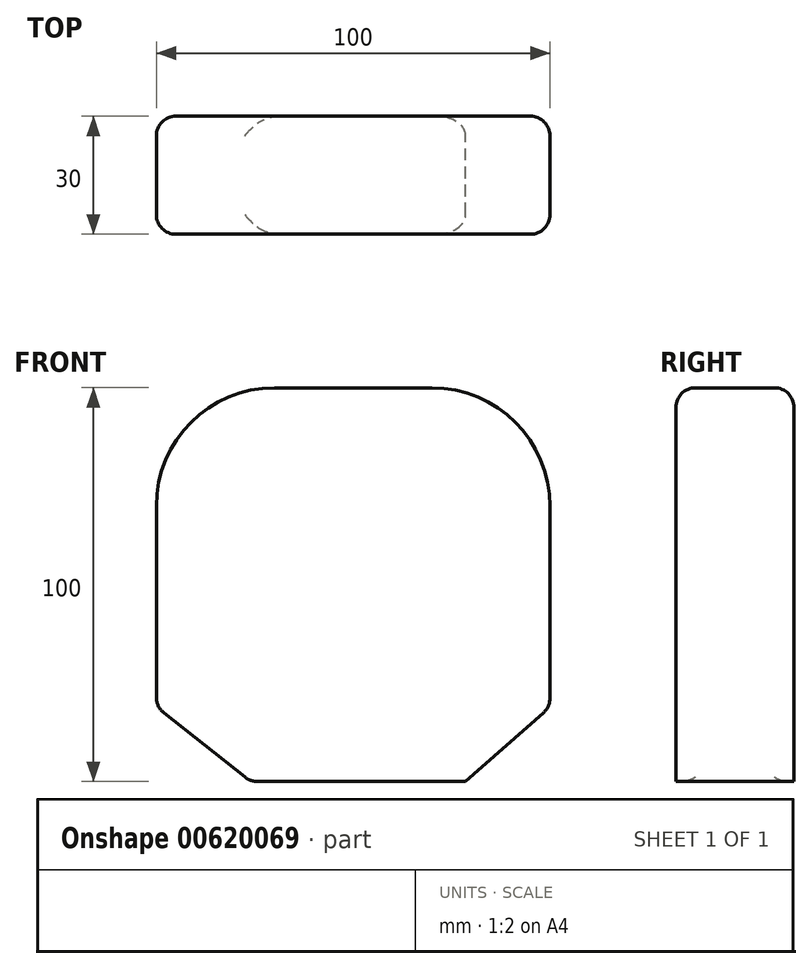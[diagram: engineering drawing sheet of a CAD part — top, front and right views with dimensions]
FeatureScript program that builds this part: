
annotation { "Feature Type Name" : "Feature", "Feature Type Description" : "" }
export const myFeature = defineFeature(function(context is Context, id is Id, definition is map)
    precondition{}
    {
        {
            var Q0;
            Q0=qCreatedBy(makeId("Front.planeOp"),FACE);
            var sketch = newSketch(context, id + "F0", { "sketchPlane" : qUnion([Q0])});
            skLineSegment(sketch, "E0.bottom", {"start": v(-36.15, 40.55) * mm, "end": v(3.85, 40.55) * mm});
            skLineSegment(sketch, "E0.top", {"start": v(-42.3, -59.45) * mm, "end": v(12.4, -59.45) * mm});
            skLineSegment(sketch, "E0.left", {"start": v(-66.15, 10.55) * mm, "end": v(-66.15, -40.55) * mm});
            skLineSegment(sketch, "E0.right", {"start": v(33.85, 10.55) * mm, "end": v(33.85, -40.55) * mm});
            skPoint(sketch, "E1.visualSharp", {"position": v(-66.15, 40.55) * mm});
            skArc(sketch, "E1.filletArc", {"start": v(-36.15, 40.55) * mm, "mid": v(-57.36, 31.76) * mm, "end": v(-66.15, 10.55) * mm});
            skPoint(sketch, "E2.visualSharp", {"position": v(33.85, 40.55) * mm});
            skArc(sketch, "E2.filletArc", {"start": v(33.85, 10.55) * mm, "mid": v(25.06, 31.76) * mm, "end": v(3.85, 40.55) * mm});
            skLineSegment(sketch, "E3", {"start": v(12.4, -59.45) * mm, "end": v(33.85, -40.55) * mm});
            skLineSegment(sketch, "E4", {"start": v(-42.3, -59.45) * mm, "end": v(-66.15, -40.55) * mm});
            skPoint(sketch, "E5.orphan", {"position": v(33.85, -59.45) * mm});
            skSolve(sketch);
        }
        {
            var Q0;
            Q0 = qSketchRegion(id + "F0", true);
            extrude(context, id + "F1", {"entities" : qUnion([Q0]), "depth" : 30 * mm, "offsetDistance" : 25 * mm});
        }
        {
            var Q0;
            Q0=makeQuery(id+"F1.opExtrude","CAP_EDGE",EDGE,{"disambiguationData":[OSD([sQuery(id+"F0.wireOp",EDGE,"E1.filletArc")])],"isStart":false});
            var Q1;
            Q1=makeQuery(id+"F1.opExtrude","SWEPT_FACE",FACE,{"disambiguationData":[OSD([sQuery(id+"F0.wireOp",EDGE,"E1.filletArc")])]});
            var Q2;
            Q2=makeQuery(id+"F1.opExtrude","CAP_EDGE",EDGE,{"disambiguationData":[OSD([sQuery(id+"F0.wireOp",EDGE,"E2.filletArc")])],"isStart":false});
            var Q3;
            Q3=makeQuery(id+"F1.opExtrude","SWEPT_FACE",FACE,{"disambiguationData":[OSD([sQuery(id+"F0.wireOp",EDGE,"E2.filletArc")])]});
            var Q4;
            Q4=makeQuery(id+"F1.opExtrude","CAP_EDGE",EDGE,{"disambiguationData":[OSD([sQuery(id+"F0.wireOp",EDGE,"E3")])],"isStart":false});
            var Q5;
            Q5=makeQuery(id+"F1.opExtrude","SWEPT_EDGE",EDGE,{"disambiguationData":[OSD([sQuery(id+"F0.wireOp",EDGE,"E0.right"),sQuery(id+"F0.wireOp",EDGE,"E3")])]});
            var Q6;
            Q6=makeQuery(id+"F1.opExtrude","CAP_EDGE",EDGE,{"disambiguationData":[OSD([sQuery(id+"F0.wireOp",EDGE,"E4")])],"isStart":false});
            var Q7;
            Q7=makeQuery(id+"F1.opExtrude","CAP_EDGE",EDGE,{"disambiguationData":[OSD([sQuery(id+"F0.wireOp",EDGE,"E4")])],"isStart":true});
            var Q8;
            Q8=makeQuery(id+"F1.opExtrude","SWEPT_FACE",FACE,{"disambiguationData":[OSD([sQuery(id+"F0.wireOp",EDGE,"E4")])]});
            var Q9;
            Q9=makeQuery(id+"F1.opExtrude","CAP_EDGE",EDGE,{"disambiguationData":[OSD([sQuery(id+"F0.wireOp",EDGE,"E3")])],"isStart":true});
            fillet(context, id + "F2", {"entities" : qUnion([Q0, Q1, Q2, Q3, Q4, Q5, Q6, Q7, Q8, Q9]), "radius" : 5 * mm, "tangentPropagation" : true, "allowEdgeOverflow" : false});
        }
    });
